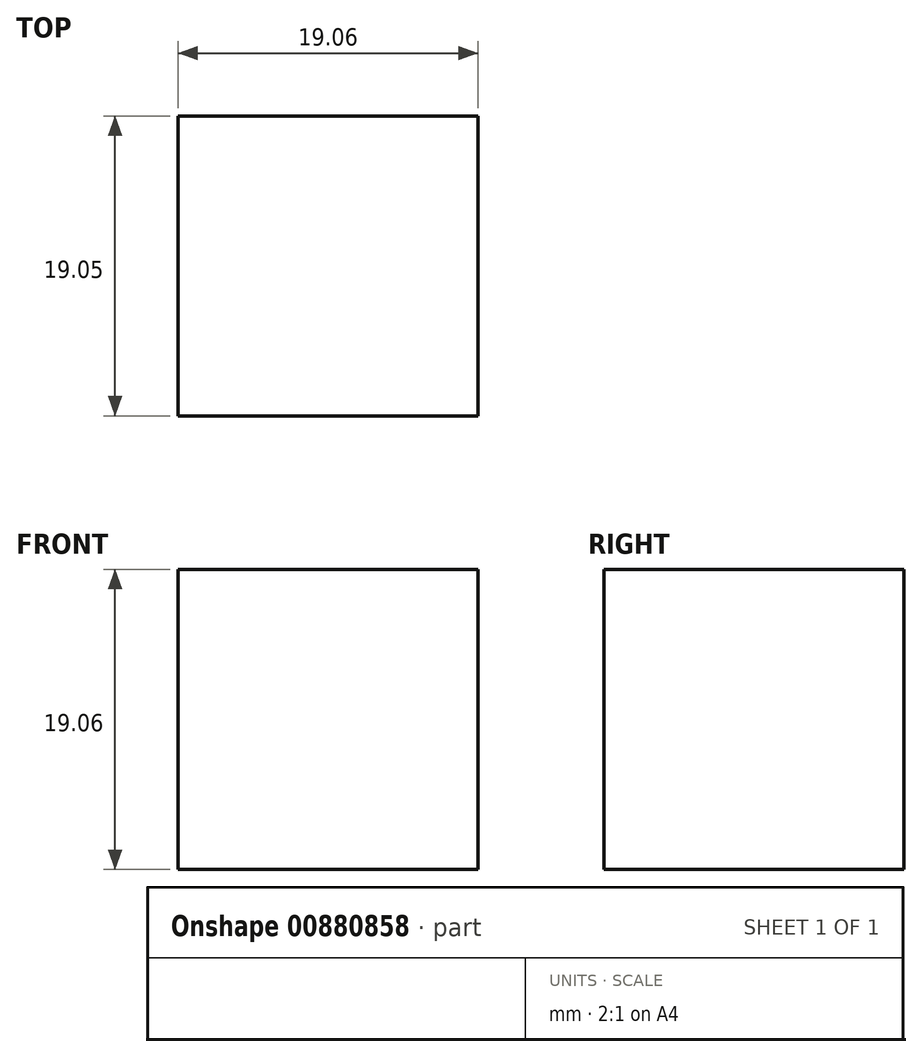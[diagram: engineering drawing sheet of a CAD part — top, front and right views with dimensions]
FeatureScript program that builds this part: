
annotation { "Feature Type Name" : "Feature", "Feature Type Description" : "" }
export const myFeature = defineFeature(function(context is Context, id is Id, definition is map)
    precondition{}
    {
        {
            var Q0;
            Q0=qCreatedBy(makeId("Front.planeOp"),FACE);
            var sketch = newSketch(context, id + "F0", { "sketchPlane" : qUnion([Q0])});
            skLineSegment(sketch, "E0.bottom", {"start": v(9.53, -9.52) * mm, "end": v(-9.53, -9.53) * mm});
            skLineSegment(sketch, "E0.top", {"start": v(9.53, 9.53) * mm, "end": v(-9.53, 9.53) * mm});
            skLineSegment(sketch, "E0.left", {"start": v(9.53, -9.52) * mm, "end": v(9.53, 9.53) * mm});
            skLineSegment(sketch, "E0.right", {"start": v(-9.53, -9.53) * mm, "end": v(-9.53, 9.53) * mm});
            skPoint(sketch, "E0.middle", {"position": v(0, 0) * mm});
            skSolve(sketch);
        }
        {
            var Q0;
            Q0=makeQuery(id+"F0.imprint","IMPRINT",FACE,{"disambiguationData":[TD([[makeQuery(id+"F0.imprint","IMPRINT",EDGE,{"derivedFrom":sQuery(id+"F0.wireOp",EDGE,"E0.bottom")}),-1.0]])]});
            extrude(context, id + "F1", {"entities" : qUnion([Q0]), "depth" : 19.05 * mm, "offsetDistance" : 25.4 * mm});
        }
    });
